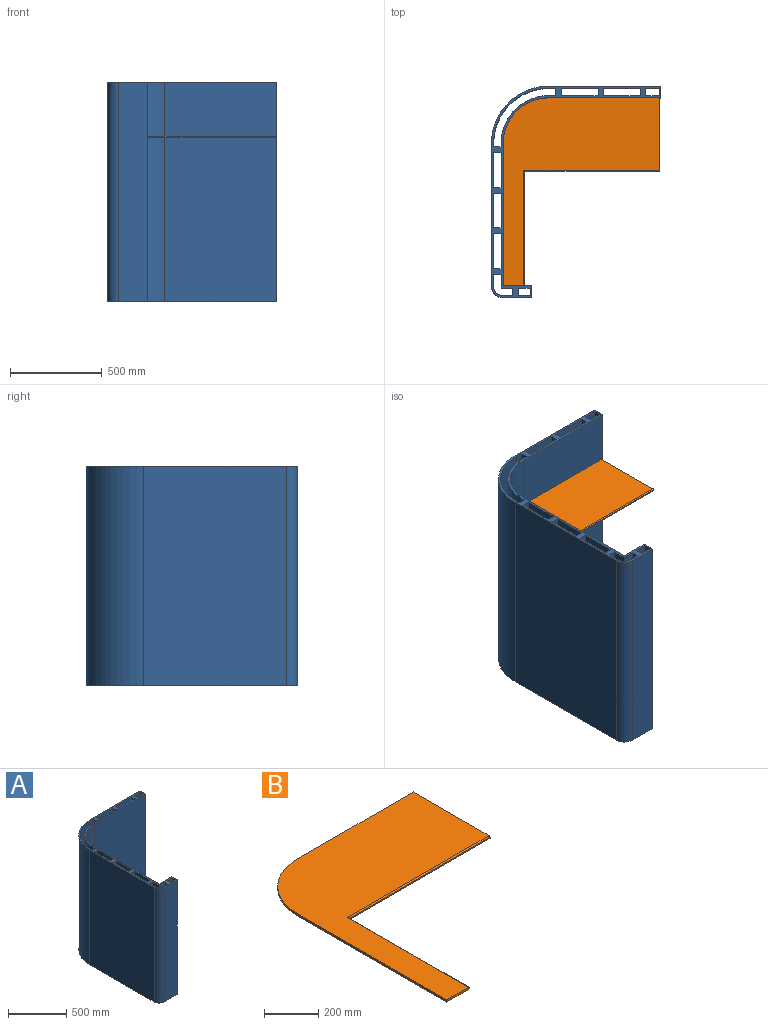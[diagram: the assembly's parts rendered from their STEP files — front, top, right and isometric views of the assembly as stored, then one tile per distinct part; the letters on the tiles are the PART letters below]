
ASSEMBLY  parts=2 mates=1
PART A: 56 faces, bbox 923x1155x1200 mm
  f0: plane 1200x65mm, normal (0,1,0), area 78000mm2, adj f18,f19,f34,f52
  f1: plane 1200x20.36mm, normal (1,0,0), area 24426mm2, adj f11,f18,f19,f33
  f2: plane 1200x192.36mm, normal (1,0,0), area 230830.2mm2, adj f18,f19,f31,f32
  f3: plane 1200x188.56mm, normal (1,0,0), area 226269mm2, adj f18,f19,f29,f30
  f4: plane 1200x194.26mm, normal (1,0,0), area 233110.8mm2, adj f18,f19,f27,f28
  f5: plane 1200x40mm, normal (0,-1,0), area 48000mm2, adj f11,f18,f19,f24
  f6: plane 1200x200mm, normal (0,-1,0), area 240000mm2, adj f18,f19,f22,f25
  f7: plane 1200x200mm, normal (0,-1,0), area 240000mm2, adj f18,f19,f20,f23
  f8: plane 1200x55mm, normal (0,1,0), area 66000mm2, adj f9,f18,f19,f35
  f9: cylinder r=50mm len=1200mm, axis (0,0,-1), area 94247.8mm2, adj f8,f10,f18,f19
  f10: plane 1200x65.47mm, normal (1,0,0), area 78563.9mm2, adj f9,f18,f19,f26
  f11: cylinder r=300mm len=1200mm, axis (0,0,-1), area 565486.7mm2, adj f1,f5,f18,f19
  f12: plane 1200x75mm, normal (0,-1,0), area 90000mm2, adj f18,f19,f21,f54
  f13: plane 1200x611mm, normal (0,1,0), area 733200mm2, adj f14,f18,f19,f55
  f14: cylinder r=312mm len=1200mm, axis (0,0,-1), area 588106.1mm2, adj f13,f15,f18,f19
  f15: plane 1200x781mm, normal (-1,0,0), area 937200mm2, adj f14,f16,f18,f19
  f16: cylinder r=62mm len=1200mm, axis (0,0,-1), area 116867.2mm2, adj f15,f17,f18,f19
  f17: plane 1200x156mm, normal (0,-1,0), area 187200mm2, adj f16,f18,f19,f53
  f18: plane 1155x923mm, normal (0,0,1), area 58939.3mm2, adj f0,f1,f2,f3,f4,f5,f6,f7
  f19: plane 1155x923mm, normal (0,0,-1), area 58939.3mm2, adj f0,f1,f2,f3,f4,f5,f6,f7
  f20: plane 1200x40mm, normal (-1,0,0), area 48000mm2, adj f7,f18,f19,f42
  f21: plane 1200x40mm, normal (1,0,0), area 48000mm2, adj f12,f18,f19,f41
  f22: plane 1200x40mm, normal (-1,0,0), area 48000mm2, adj f6,f18,f19,f43
  f23: plane 1200x40mm, normal (1,0,0), area 48000mm2, adj f7,f18,f19,f42
  f24: plane 1200x40mm, normal (-1,0,0), area 48000mm2, adj f5,f18,f19,f50
  f25: plane 1200x40mm, normal (1,0,0), area 48000mm2, adj f6,f18,f19,f43
  f26: plane 1200x40mm, normal (0,-1,0), area 48000mm2, adj f10,f18,f19,f36
  f27: plane 1200x40mm, normal (0,1,0), area 48000mm2, adj f4,f18,f19,f37
  f28: plane 1200x40mm, normal (0,-1,0), area 48000mm2, adj f4,f18,f19,f37
  f29: plane 1200x40mm, normal (0,1,0), area 48000mm2, adj f3,f18,f19,f38
  f30: plane 1200x40mm, normal (0,-1,0), area 48000mm2, adj f3,f18,f19,f38
  f31: plane 1200x40mm, normal (0,1,0), area 48000mm2, adj f2,f18,f19,f39
  f32: plane 1200x40mm, normal (0,-1,0), area 48000mm2, adj f2,f18,f19,f39
  f33: plane 1200x40mm, normal (0,1,0), area 48000mm2, adj f1,f18,f19,f44
  f34: plane 1200x40mm, normal (1,0,0), area 48000mm2, adj f0,f18,f19,f45
  f35: plane 1200x40mm, normal (-1,0,0), area 48000mm2, adj f8,f18,f19,f40
  f36: plane 1200x75.47mm, normal (-1,0,0), area 90563.9mm2, adj f18,f19,f26,f40
  f37: plane 1200x194.26mm, normal (-1,0,0), area 233110.8mm2, adj f18,f19,f27,f28
  f38: plane 1200x188.56mm, normal (-1,0,0), area 226269mm2, adj f18,f19,f29,f30
  f39: plane 1200x192.36mm, normal (-1,0,0), area 230830.2mm2, adj f18,f19,f31,f32
  f40: plane 1200x65mm, normal (0,-1,0), area 78000mm2, adj f18,f19,f35,f36
  f41: plane 1200x75mm, normal (0,1,0), area 90000mm2, adj f18,f19,f21,f54
  f42: plane 1200x200mm, normal (0,1,0), area 240000mm2, adj f18,f19,f20,f23
  f43: plane 1200x200mm, normal (0,1,0), area 240000mm2, adj f18,f19,f22,f25
  f44: plane 1200x20.36mm, normal (-1,0,0), area 24426mm2, adj f18,f19,f33,f51
  f45: plane 1200x65mm, normal (0,-1,0), area 78000mm2, adj f18,f19,f34,f52
  f46: plane 1200x154mm, normal (0,1,0), area 184800mm2, adj f18,f19,f47,f53
  f47: plane 1200x779mm, normal (1,0,0), area 934800mm2, adj f18,f19,f46,f48
  f48: cylinder r=248mm len=1200mm, axis (0,0,-1), area 467469mm2, adj f18,f19,f47,f49
  f49: plane 1200x611mm, normal (0,-1,0), area 733200mm2, adj f18,f19,f48,f55
  f50: plane 1200x40mm, normal (0,1,0), area 48000mm2, adj f18,f19,f24,f51
  f51: cylinder r=260mm len=1200mm, axis (0,0,-1), area 490088.5mm2, adj f18,f19,f44,f50
  f52: plane 1200x40mm, normal (-1,0,0), area 48000mm2, adj f0,f18,f19,f45
  f53: plane 1200x64mm, normal (1,0,0), area 76800mm2, adj f17,f18,f19,f46
  f54: plane 1200x40mm, normal (-1,0,0), area 48000mm2, adj f12,f18,f19,f41
  f55: plane 1200x64mm, normal (1,0,0), area 76800mm2, adj f13,f18,f19,f49
PART B: 11 faces, bbox 853x1027x10 mm
  f0: plane 605x10mm, normal (0,1,0), area 6050mm2, adj f1,f6,f7,f8
  f1: cylinder r=248mm len=248mm, axis (0,0,-1), area 3895.6mm2, adj f0,f2,f7,f8
  f2: plane 779x10mm, normal (-1,0,0), area 7790mm2, adj f1,f3,f7,f8
  f3: plane 118x10mm, normal (0,-1,0), area 1174.6mm2, adj f2,f4,f7,f8,f9
  f4: plane 627x5mm, normal (1,0,0), area 3135mm2, adj f3,f5,f8,f9
  f5: plane 735x5mm, normal (0,-1,0), area 3675mm2, adj f4,f6,f8,f10
  f6: plane 400x10mm, normal (1,0,0), area 3994.6mm2, adj f0,f5,f7,f8,f10
  f7: plane 1027x853mm, normal (0,0,1), area 395152.1mm2, adj f0,f1,f2,f3,f6,f9,f10
  f8: plane 1027x853mm, normal (0,0,-1), area 401987.1mm2, adj f0,f1,f2,f3,f4,f5,f6
  f9: cylinder r=5mm len=632mm, axis (0,-1,0), area 4938.7mm2, adj f3,f4,f7,f10
  f10: cylinder r=5mm len=740mm, axis (-1,0,0), area 5786.9mm2, adj f5,f6,f7,f9
PLACE A t=(-861.01,597.82,-537.45)mm
PLACE B t=(-561.01,297.82,357.55)mm
MATE slider B.f2 <-> A.f47  axis (-1,0,0) through (-809.01,-91.68,362.55)mm
